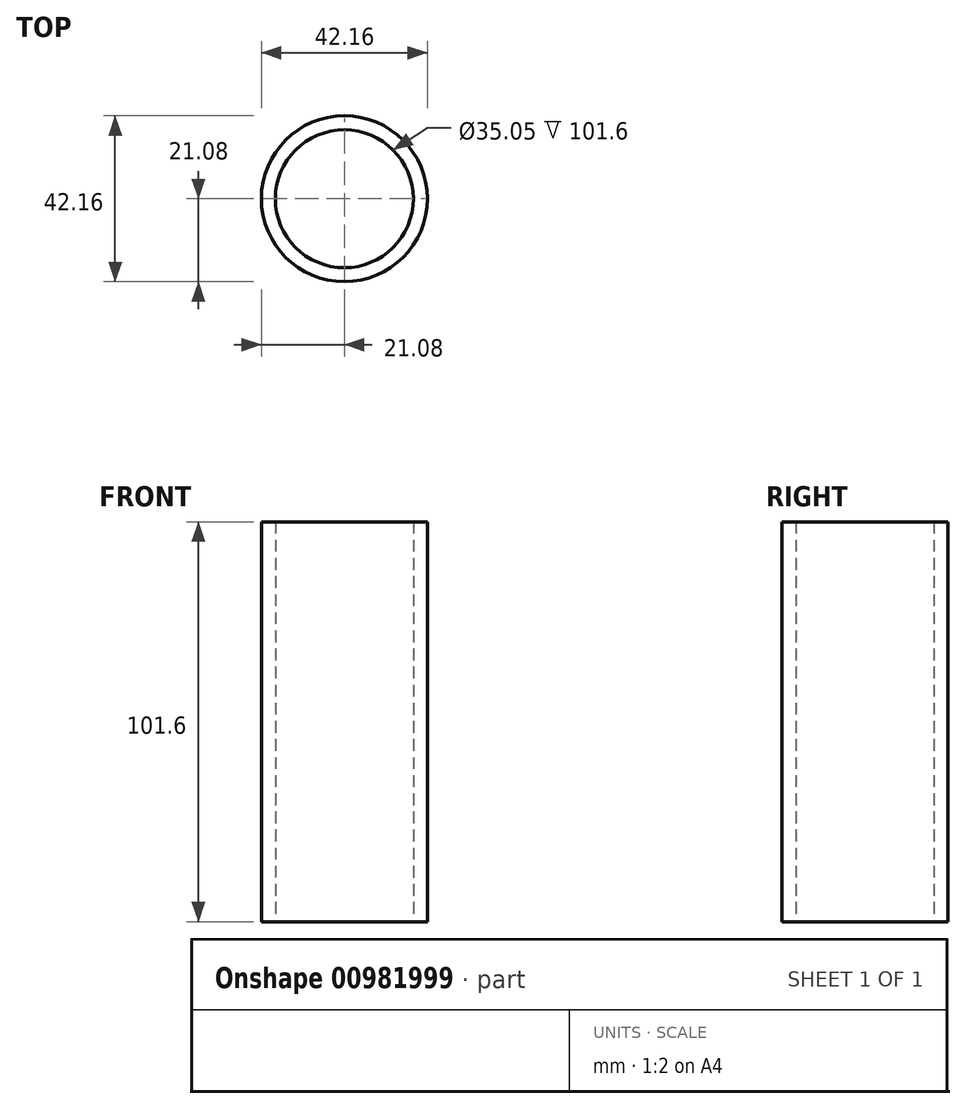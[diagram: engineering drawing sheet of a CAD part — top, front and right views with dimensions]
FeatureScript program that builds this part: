
annotation { "Feature Type Name" : "Feature", "Feature Type Description" : "" }
export const myFeature = defineFeature(function(context is Context, id is Id, definition is map)
    precondition{}
    {
        {
            var Q0;
            Q0=qCreatedBy(makeId("Top.planeOp"),FACE);
            var sketch = newSketch(context, id + "F0", { "sketchPlane" : qUnion([Q0])});
            skCircle(sketch, "E0", {"center": v(0, 0) * mm, "radius": 17.53 * mm});
            skCircle(sketch, "E1", {"center": v(0, 0) * mm, "radius": 21.08 * mm});
            skSolve(sketch);
        }
        {
            var Q0;
            Q0=qSketchRegion(id+"F0",true);
            extrude(context, id + "F1", {"entities" : qUnion([Q0]), "depth" : 101.6 * mm, "offsetDistance" : 25.4 * mm});
        }
    });
